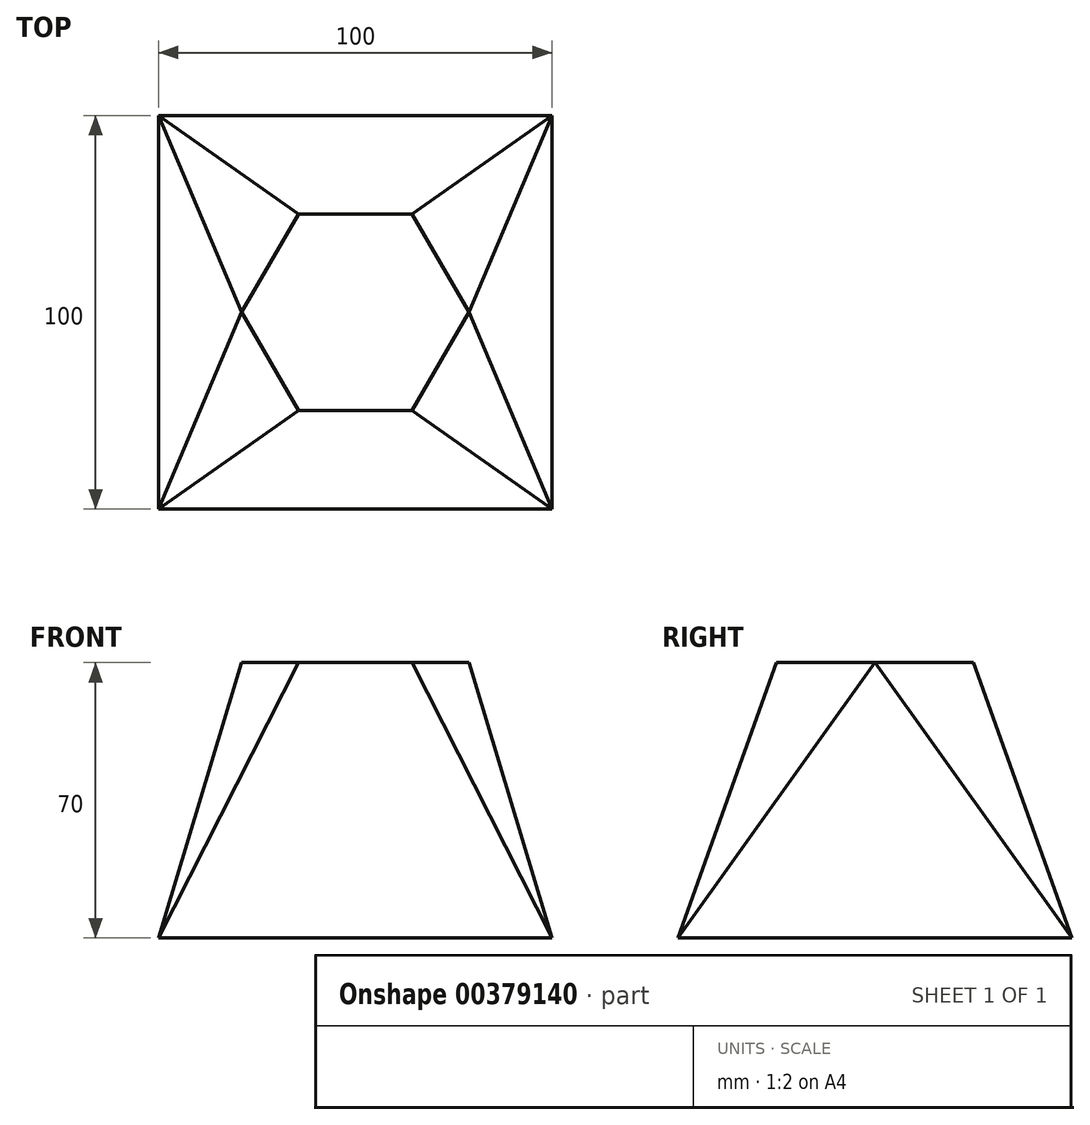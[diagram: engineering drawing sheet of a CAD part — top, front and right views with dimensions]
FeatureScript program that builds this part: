
annotation { "Feature Type Name" : "Feature", "Feature Type Description" : "" }
export const myFeature = defineFeature(function(context is Context, id is Id, definition is map)
    precondition{}
    {
        {
            var Q0;
            Q0=qCreatedBy(makeId("Top.planeOp"),FACE);
            var sketch = newSketch(context, id + "F0", { "sketchPlane" : qUnion([Q0])});
            skLineSegment(sketch, "E0.bottom", {"start": v(50, 50) * mm, "end": v(-50, 50) * mm});
            skLineSegment(sketch, "E0.top", {"start": v(50, -50) * mm, "end": v(-50, -50) * mm});
            skLineSegment(sketch, "E0.left", {"start": v(50, 50) * mm, "end": v(50, -50) * mm});
            skLineSegment(sketch, "E0.right", {"start": v(-50, 50) * mm, "end": v(-50, -50) * mm});
            skPoint(sketch, "E0.middle", {"position": v(0, 0) * mm});
            skSolve(sketch);
        }
        {
            var Q0;
            Q0=qCreatedBy(makeId("Top.planeOp"),FACE);
            cPlane(context, id + "F1", {"entities" : qUnion([Q0]), "cplaneType" : CPlaneType.OFFSET, "offset" : 70 * mm, "width" : 150 * mm, "height" : 150 * mm});
        }
        {
            var Q0;
            Q0=qCreatedBy(id+"F1.planeOp",FACE);
            var sketch = newSketch(context, id + "F2", { "sketchPlane" : qUnion([Q0])});
            skCircle(sketch, "E1.cCircle", {"center": v(0, 0) * mm, "radius": 25 * mm, "construction": true});
            skLineSegment(sketch, "E1.0", {"start": v(-14.43, 25) * mm, "end": v(14.43, 25) * mm});
            skLineSegment(sketch, "E1.1", {"start": v(14.43, 25) * mm, "end": v(28.87, 0) * mm});
            skLineSegment(sketch, "E1.2", {"start": v(28.87, 0) * mm, "end": v(14.43, -25) * mm});
            skLineSegment(sketch, "E1.3", {"start": v(14.43, -25) * mm, "end": v(-14.43, -25) * mm});
            skLineSegment(sketch, "E1.4", {"start": v(-14.43, -25) * mm, "end": v(-28.87, 0) * mm});
            skLineSegment(sketch, "E1.5", {"start": v(-28.87, 0) * mm, "end": v(-14.43, 25) * mm});
            skPoint(sketch, "E1.0.midPoint", {"position": v(0, 25) * mm});
            skLineSegment(sketch, "E2", {"start": v(-14.43, 25) * mm, "end": v(-14.43, -25) * mm});
            skLineSegment(sketch, "E3", {"start": v(14.43, 25) * mm, "end": v(14.43, -25) * mm});
            skSolve(sketch);
        }
        {
            var Q0;
            Q0=makeQuery(id+"F2.imprint","IMPRINT",FACE,{"disambiguationData":[TD([[makeQuery(id+"F2.imprint","IMPRINT",EDGE,{"derivedFrom":sQuery(id+"F2.wireOp",EDGE,"E1.0")}),-1.0]])]});
            var Q1;
            Q1=makeQuery(id+"F0.imprint","IMPRINT",FACE,{"disambiguationData":[TD([[makeQuery(id+"F0.imprint","IMPRINT",EDGE,{"derivedFrom":sQuery(id+"F0.wireOp",EDGE,"E0.bottom")}),1.0]])]});
            loft(context, id + "F3", {"sheetProfilesArray" : [{ "sheetProfileEntities" : qUnion([Q0]) }, { "sheetProfileEntities" : qUnion([Q1]) }]});
        }
        {
            var Q1;
            Q1=makeQuery(id+"F2.imprint","IMPRINT",FACE,{"disambiguationData":[TD([[makeQuery(id+"F2.imprint","IMPRINT",EDGE,{"derivedFrom":sQuery(id+"F2.wireOp",EDGE,"E1.1")}),-1.0]])]});
            var Q2;
            Q2=makeQuery(id+"F3.opLoft","MID_CAP_VERTEX",VERTEX,{"disambiguationData":[OSD([sQuery(id+"F0.wireOp",EDGE,"E0.top"),sQuery(id+"F0.wireOp",EDGE,"E0.left")])],"capPos":1.0});
            loft(context, id + "F4", {"operationType" : NewBodyOperationType.ADD, "sheetProfilesArray" : [{ "sheetProfileEntities" : qUnion([Q1]) }, { "sheetProfileEntities" : qUnion([Q2]) }]});
        }
        {
            var Q1;
            Q1=makeQuery(id+"F2.imprint","IMPRINT",FACE,{"disambiguationData":[TD([[makeQuery(id+"F2.imprint","IMPRINT",EDGE,{"derivedFrom":sQuery(id+"F2.wireOp",EDGE,"E1.1")}),-1.0]])]});
            var Q2;
            Q2=makeQuery(id+"F3.opLoft","MID_CAP_VERTEX",VERTEX,{"disambiguationData":[OSD([sQuery(id+"F0.wireOp",EDGE,"E0.bottom"),sQuery(id+"F0.wireOp",EDGE,"E0.left")])],"capPos":1.0});
            loft(context, id + "F5", {"operationType" : NewBodyOperationType.ADD, "sheetProfilesArray" : [{ "sheetProfileEntities" : qUnion([Q1]) }, { "sheetProfileEntities" : qUnion([Q2]) }]});
        }
        {
            var Q1;
            Q1=makeQuery(id+"F2.imprint","IMPRINT",FACE,{"disambiguationData":[TD([[makeQuery(id+"F2.imprint","IMPRINT",EDGE,{"derivedFrom":sQuery(id+"F2.wireOp",EDGE,"E1.4")}),-1.0]])]});
            var Q2;
            Q2=makeQuery(id+"F3.opLoft","MID_CAP_VERTEX",VERTEX,{"disambiguationData":[OSD([sQuery(id+"F0.wireOp",EDGE,"E0.bottom"),sQuery(id+"F0.wireOp",EDGE,"E0.right")])],"capPos":1.0});
            loft(context, id + "F6", {"operationType" : NewBodyOperationType.ADD, "sheetProfilesArray" : [{ "sheetProfileEntities" : qUnion([Q1]) }, { "sheetProfileEntities" : qUnion([Q2]) }]});
        }
        {
            var Q1;
            Q1=makeQuery(id+"F2.imprint","IMPRINT",FACE,{"disambiguationData":[TD([[makeQuery(id+"F2.imprint","IMPRINT",EDGE,{"derivedFrom":sQuery(id+"F2.wireOp",EDGE,"E1.4")}),-1.0]])]});
            var Q2;
            Q2=makeQuery(id+"F3.opLoft","MID_CAP_VERTEX",VERTEX,{"disambiguationData":[OSD([sQuery(id+"F0.wireOp",EDGE,"E0.top"),sQuery(id+"F0.wireOp",EDGE,"E0.right")])],"capPos":1.0});
            loft(context, id + "F7", {"operationType" : NewBodyOperationType.ADD, "sheetProfilesArray" : [{ "sheetProfileEntities" : qUnion([Q1]) }, { "sheetProfileEntities" : qUnion([Q2]) }]});
        }
        {
            var Q1;
            Q1=makeQuery(id+"F6.opLoft","SWEPT_FACE",FACE,{"disambiguationData":[OSD([sQuery(id+"F2.wireOp",EDGE,"E1.3"),sQuery(id+"F2.wireOp",EDGE,"E1.4"),sQuery(id+"F2.wireOp",EDGE,"E1.5"),sQuery(id+"F2.wireOp",EDGE,"E2")])]});
            var Q2;
            Q2=makeQuery(id+"F7.opLoft","SWEPT_FACE",FACE,{"disambiguationData":[OSD([sQuery(id+"F2.wireOp",EDGE,"E1.0"),sQuery(id+"F2.wireOp",EDGE,"E1.4"),sQuery(id+"F2.wireOp",EDGE,"E1.5"),sQuery(id+"F2.wireOp",EDGE,"E2")])]});
            var Q3;
            Q3=makeQuery(id+"F3.opLoft","MID_CAP_EDGE",EDGE,{"disambiguationData":[OSD([sQuery(id+"F0.wireOp",EDGE,"E0.bottom"),sQuery(id+"F0.wireOp",EDGE,"E0.top"),sQuery(id+"F0.wireOp",EDGE,"E0.right")])],"capPos":1.0});
            loft(context, id + "F8", {"operationType" : NewBodyOperationType.ADD, "addGuides" : true, "sheetProfilesArray" : [{ "sheetProfileEntities" : qUnion([Q1]) }, { "sheetProfileEntities" : qUnion([Q2]) }], "guidesArray" : [{ "guideEntities" : qUnion([Q3]), "guideDerivativeType" : LoftGuideDerivativeType.DEFAULT, "guideDerivativeMagnitude" : 1 }]});
        }
        {
            var Q1;
            Q1=makeQuery(id+"F4.opLoft","SWEPT_FACE",FACE,{"disambiguationData":[OSD([sQuery(id+"F2.wireOp",EDGE,"E1.0"),sQuery(id+"F2.wireOp",EDGE,"E1.1"),sQuery(id+"F2.wireOp",EDGE,"E1.2"),sQuery(id+"F2.wireOp",EDGE,"E3")])]});
            var Q2;
            Q2=makeQuery(id+"F5.opLoft","SWEPT_FACE",FACE,{"disambiguationData":[OSD([sQuery(id+"F2.wireOp",EDGE,"E1.1"),sQuery(id+"F2.wireOp",EDGE,"E1.2"),sQuery(id+"F2.wireOp",EDGE,"E1.3"),sQuery(id+"F2.wireOp",EDGE,"E3")])]});
            var Q3;
            Q3=makeQuery(id+"F3.opLoft","MID_CAP_EDGE",EDGE,{"disambiguationData":[OSD([sQuery(id+"F0.wireOp",EDGE,"E0.bottom"),sQuery(id+"F0.wireOp",EDGE,"E0.top"),sQuery(id+"F0.wireOp",EDGE,"E0.left")])],"capPos":1.0});
            loft(context, id + "F9", {"operationType" : NewBodyOperationType.ADD, "addGuides" : true, "sheetProfilesArray" : [{ "sheetProfileEntities" : qUnion([Q1]) }, { "sheetProfileEntities" : qUnion([Q2]) }], "guidesArray" : [{ "guideEntities" : qUnion([Q3]), "guideDerivativeType" : LoftGuideDerivativeType.DEFAULT, "guideDerivativeMagnitude" : 1 }]});
        }
    });
